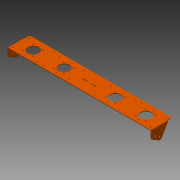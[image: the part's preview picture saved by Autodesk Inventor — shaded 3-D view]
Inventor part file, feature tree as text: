
AUTODESK INVENTOR PART (.ipt)
format: ipt  version: 2013 SP2 (Build 170200200, 200)  size: 390,656 bytes
history: native  units: mm
features: sketch x8, other x5, sheet_metal_op x4, hole x4, chamfer x2, plane x2, mirror x2, pattern_linear x1
ambient origin geometry x8: Origin, YZ Plane, XZ Plane, XY Plane, X Axis, Y Axis, Z Axis, Center Point
bodies: Solid1 (feature_tree)
feature tree (28):
  sheet_metal_op  "Face1"
  sheet_metal_op  "Flange1"
  hole  "Hole1"  [1 undecoded]
  chamfer  "Corner Round1"
  plane  "Work Plane1"
  mirror  "Mirror1"
  hole  "Hole3"  [1 undecoded]
  hole  "Hole4"  [1 undecoded]
  pattern_linear  "Rectangular Pattern1"  Count1=5 Spacing1=90.0deg
  plane  "Work Plane2"
  mirror  "Mirror2"
  hole  "Hole5"  [1 undecoded]
  chamfer  "Corner Round3"
  sketch  "Sketch1"  dims[d0=458.0mm d2=69.0mm]
  other  "Plate1"
  sketch  "Sketch2"  dims[d3=2.0mm d4=2.0mm]
  other  "Plate2"
  sheet_metal_op  "Bend1"
  sheet_metal_op  "Corner1"
  sketch  "Sketch4"  dims[d5=1.0mm d6=4.0mm]
  sketch  "Sketch5"  dims[d7=2.0mm d8=50.0mm d9=90.0deg d10=1.0mm]
  sketch  "Sketch8"  dims[d11=8.0mm d12=2.0mm]
  sketch  "Sketch9"  dims[d13=2.0mm]
  sketch  "Sketch10"  dims[d14=0.0mm d15=15.0mm]
  sketch  "Sketch11"  dims[d22=90.0deg d23=20.0mm d24=30.0deg d25=2.0mm d26=0.0mm d29=15.0mm d30=4.5mm d31=6.0mm d32=4.0mm d33=2.0mm d34=90.0deg d35=2.0mm d36=20.594885mm d39=10.0mm d40=10.0mm d41=6.0mm d71=7.5mm d72=10.0mm d73=30.0mm d75=40.0mm d76=20.0mm d78=51.0mm d81=3.4mm d82=6.0mm d83=4.0mm d84=2.0mm d85=90.0deg d86=2.0mm d87=20.594885mm d88=35.0mm d89=2.0mm d90=0.0mm d91=32.0mm d92=32.0mm d93=3.4mm d94=6.0mm d95=6.0mm d96=2.0mm d97=90.0deg d98=2.0mm d99=20.594885mm d100=20.0mm d102=99.0mm d103=36.0mm d104=19.0mm d105=10.0mm d106=19.0mm d107=10.0mm d108=6.2mm d109=6.0mm d110=4.0mm d111=2.0mm d112=90.0deg d113=2.0mm d114=20.594885mm d115=6.0mm]
  other  "Cut2"
  other  "Cut4"
  other  "Definition1"
note: 4 required parameter values undecoded (feature->parameter linkage not recoverable at this tier; creation-order binding heuristic only, values carry confidence <= 0.55)
